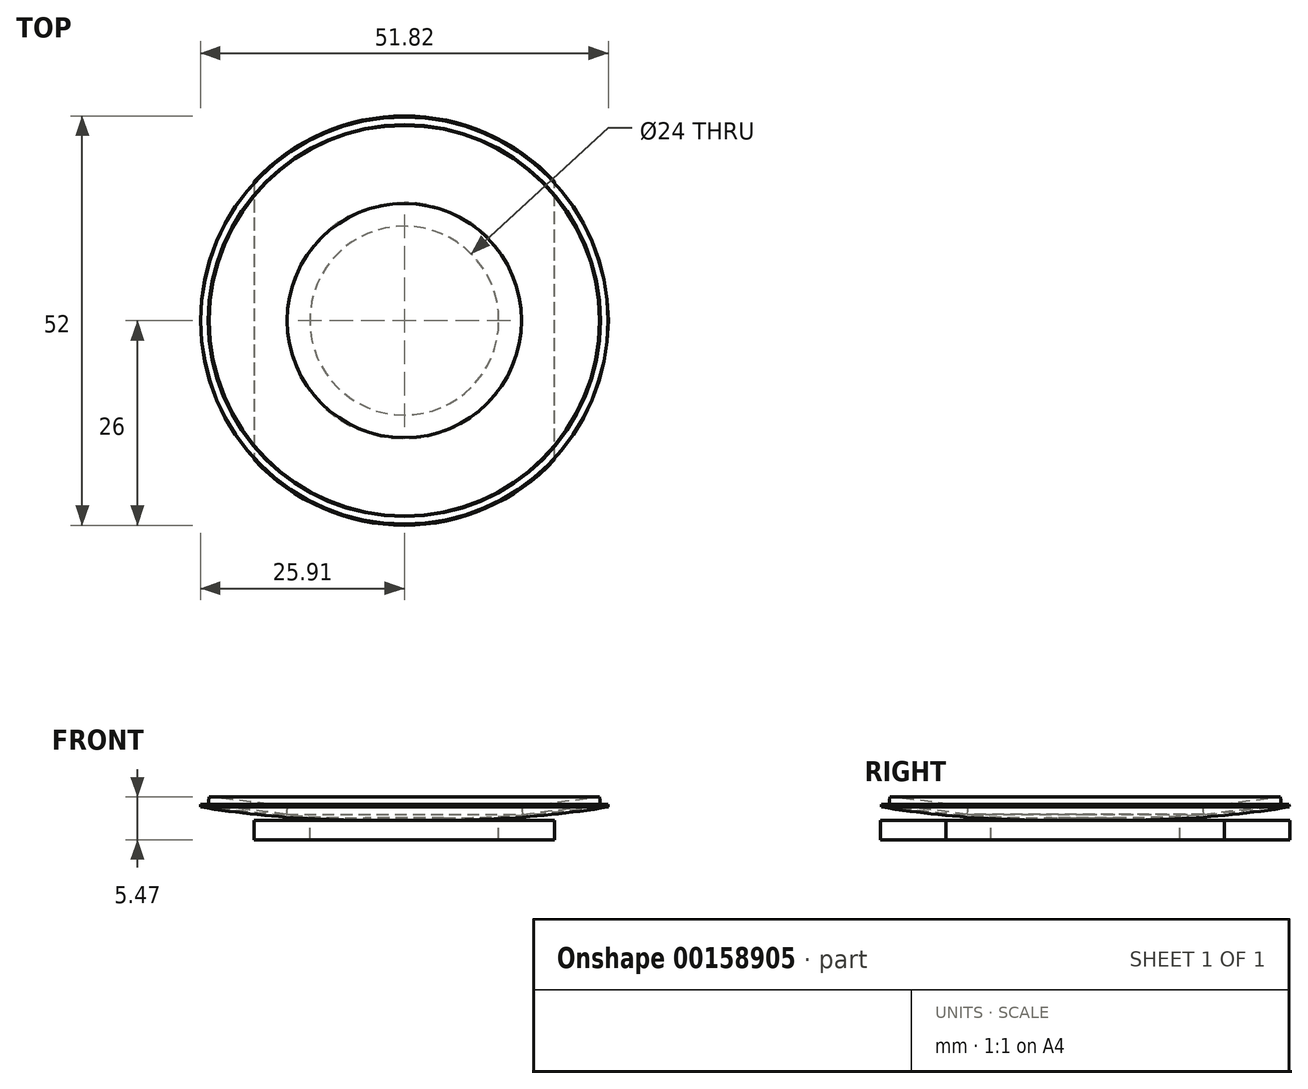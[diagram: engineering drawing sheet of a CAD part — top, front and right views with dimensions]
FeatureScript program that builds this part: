
annotation { "Feature Type Name" : "Feature", "Feature Type Description" : "" }
export const myFeature = defineFeature(function(context is Context, id is Id, definition is map)
    precondition{}
    {
        {
            var Q0;
            Q0=qCreatedBy(makeId("Top.planeOp"),FACE);
            var sketch = newSketch(context, id + "F0", { "sketchPlane" : qUnion([Q0])});
            skCircle(sketch, "E0", {"center": v(0, 0) * mm, "radius": 25 * mm});
            skLineSegment(sketch, "E1.bottom", {"start": v(-17.68, 28.98) * mm, "end": v(17.68, 28.98) * mm});
            skLineSegment(sketch, "E1.top", {"start": v(-17.68, -26.82) * mm, "end": v(17.68, -26.82) * mm});
            skLineSegment(sketch, "E1.left", {"start": v(-17.68, 28.98) * mm, "end": v(-17.68, -26.82) * mm});
            skLineSegment(sketch, "E1.right", {"start": v(17.68, 28.98) * mm, "end": v(17.68, -26.82) * mm});
            skCircle(sketch, "E2", {"center": v(0, 0) * mm, "radius": 15 * mm});
            skLineSegment(sketch, "E3", {"start": v(-17.68, 17.68) * mm, "end": v(0, 0) * mm});
            skLineSegment(sketch, "E4", {"start": v(0, 0) * mm, "end": v(17.68, 17.68) * mm});
            skLineSegment(sketch, "E5", {"start": v(0, 0) * mm, "end": v(-17.68, -17.68) * mm});
            skLineSegment(sketch, "E6", {"start": v(0, 0) * mm, "end": v(17.68, -17.68) * mm});
            skSolve(sketch);
        }
        {
            var Q0;
            Q0=qCreatedBy(makeId("Top.planeOp"),FACE);
            var sketch = newSketch(context, id + "F1", { "sketchPlane" : qUnion([Q0])});
            skArc(sketch, "E7.0", {"start": v(0, 26) * mm, "mid": v(-10.4, 23.83) * mm, "end": v(-19.08, 17.66) * mm});
            skPoint(sketch, "E8.visualSharp", {"position": v(0, 4.3) * mm});
            skCircle(sketch, "E9", {"center": v(0, 0) * mm, "radius": 12 * mm});
            skLineSegment(sketch, "E10", {"start": v(-19.08, 17.66) * mm, "end": v(-19.08, 0) * mm});
            skArc(sketch, "E11.MirrorCS", {"start": v(0, 26) * mm, "mid": v(10.4, 23.83) * mm, "end": v(19.08, 17.66) * mm});
            skLineSegment(sketch, "E12.MirrorCS", {"start": v(19.08, 17.66) * mm, "end": v(19.08, 0) * mm});
            skLineSegment(sketch, "E13.MirrorCS", {"start": v(-19.08, -17.66) * mm, "end": v(-19.08, 0) * mm});
            skArc(sketch, "E14.MirrorCS", {"start": v(0, -26) * mm, "mid": v(-10.4, -23.83) * mm, "end": v(-19.08, -17.66) * mm});
            skArc(sketch, "E15.MirrorCS", {"start": v(0, -26) * mm, "mid": v(10.4, -23.83) * mm, "end": v(19.08, -17.66) * mm});
            skLineSegment(sketch, "E16.MirrorCS", {"start": v(19.08, -17.66) * mm, "end": v(19.08, 0) * mm});
            skSolve(sketch);
        }
        {
            var Q0;
            Q0=qSketchRegion(id+"F1",true);
            extrude(context, id + "F2", {"entities" : qUnion([Q0]), "oppositeDirection" : true, "depth" : 0.5 * mm});
        }
        {
            var Q0;
            Q0=makeQuery(id+"F2.opExtrude","CAP_FACE",FACE,{"disambiguationData":[OSD([sQuery(id+"F1.wireOp",EDGE,"E9"),sQuery(id+"F1.wireOp",EDGE,"E11.MirrorCS"),sQuery(id+"F1.wireOp",EDGE,"E7.0"),sQuery(id+"F1.wireOp",EDGE,"E10"),sQuery(id+"F1.wireOp",EDGE,"E12.MirrorCS"),sQuery(id+"F1.wireOp",EDGE,"E13.MirrorCS"),sQuery(id+"F1.wireOp",EDGE,"E14.MirrorCS"),sQuery(id+"F1.wireOp",EDGE,"E15.MirrorCS"),sQuery(id+"F1.wireOp",EDGE,"E16.MirrorCS")])],"isStart":false});
            extrude(context, id + "F3", {"entities" : qUnion([Q0]), "operationType" : NewBodyOperationType.ADD, "depth" : 2 * mm});
        }
        {
            var Q0;
            Q0=qCreatedBy(makeId("Right.planeOp"),FACE);
            var sketch = newSketch(context, id + "F4", { "sketchPlane" : qUnion([Q0])});
            skLineSegment(sketch, "E17", {"start": v(0, 13.4) * mm, "end": v(0, -10.8) * mm});
            skLineSegment(sketch, "E18", {"start": v(-26, 0) * mm, "end": v(-25.64, 6.58) * mm, "construction": true});
            skLineSegment(sketch, "E19", {"start": v(0, 0) * mm, "end": v(-5, 0) * mm});
            skArc(sketch, "E20", {"start": v(-5, 0) * mm, "mid": v(-15.49, 0.42) * mm, "end": v(-25.9, 1.69) * mm});
            skArc(sketch, "E21.0", {"start": v(-5, 0.3) * mm, "mid": v(-15.46, 0.72) * mm, "end": v(-25.86, 1.98) * mm});
            skLineSegment(sketch, "E22", {"start": v(-5, 0.3) * mm, "end": v(0, 0.3) * mm});
            skLineSegment(sketch, "E23", {"start": v(0, 0.3) * mm, "end": v(0, 0) * mm});
            skLineSegment(sketch, "E24", {"start": v(-25.86, 1.98) * mm, "end": v(-25.9, 1.69) * mm});
            skLineSegment(sketch, "E25", {"start": v(-25.86, 1.98) * mm, "end": v(-15.78, 0.75) * mm});
            skLineSegment(sketch, "E26", {"start": v(-15.78, 0.75) * mm, "end": v(-15.64, 1.84) * mm});
            skLineSegment(sketch, "E27", {"start": v(-15.64, 1.84) * mm, "end": v(-25.73, 3.08) * mm});
            skLineSegment(sketch, "E28", {"start": v(-25.73, 3.08) * mm, "end": v(-25.86, 1.98) * mm});
            skSolve(sketch);
        }
        {
            var Q0;
            Q0=makeQuery(id+"F4.imprint","IMPRINT",FACE,{"disambiguationData":[TD([[makeQuery(id+"F4.imprint","IMPRINT",EDGE,{"derivedFrom":sQuery(id+"F4.wireOp",EDGE,"E19")}),-1.0]])]});
            var Q1;
            Q1=sQuery(id+"F4.wireOp",EDGE,"E17");
            revolve(context, id + "F5", {"entities" : qUnion([Q0]), "axis" : qUnion([Q1]), "revolveType" : RevolveType.FULL});
        }
        {
            var Q0;
            Q0=qCreatedBy(makeId("Right.planeOp"),FACE);
            var sketch = newSketch(context, id + "F6", { "sketchPlane" : qUnion([Q0])});
            skLineSegment(sketch, "E29", {"start": v(-24.9, 1.97) * mm, "end": v(-24.8, 2.97) * mm});
            skLineSegment(sketch, "E30", {"start": v(-24.8, 2.97) * mm, "end": v(-14.88, 1.75) * mm});
            skLineSegment(sketch, "E31", {"start": v(-14.88, 1.75) * mm, "end": v(-15, 0.76) * mm});
            skLineSegment(sketch, "E32", {"start": v(-15, 0.76) * mm, "end": v(-24.9, 1.97) * mm});
            skLineSegment(sketch, "E33", {"start": v(0, 0) * mm, "end": v(0, 0.9) * mm});
            skSolve(sketch);
        }
        {
            var Q0;
            Q0=makeQuery(id+"F6.imprint","IMPRINT",FACE,{"disambiguationData":[TD([[makeQuery(id+"F6.imprint","IMPRINT",EDGE,{"derivedFrom":sQuery(id+"F6.wireOp",EDGE,"E29")}),-1.0]])]});
            var Q1;
            Q1=sQuery(id+"F6.wireOp",EDGE,"E33");
            revolve(context, id + "F7", {"entities" : qUnion([Q0]), "axis" : qUnion([Q1]), "revolveType" : RevolveType.FULL});
        }
    });
